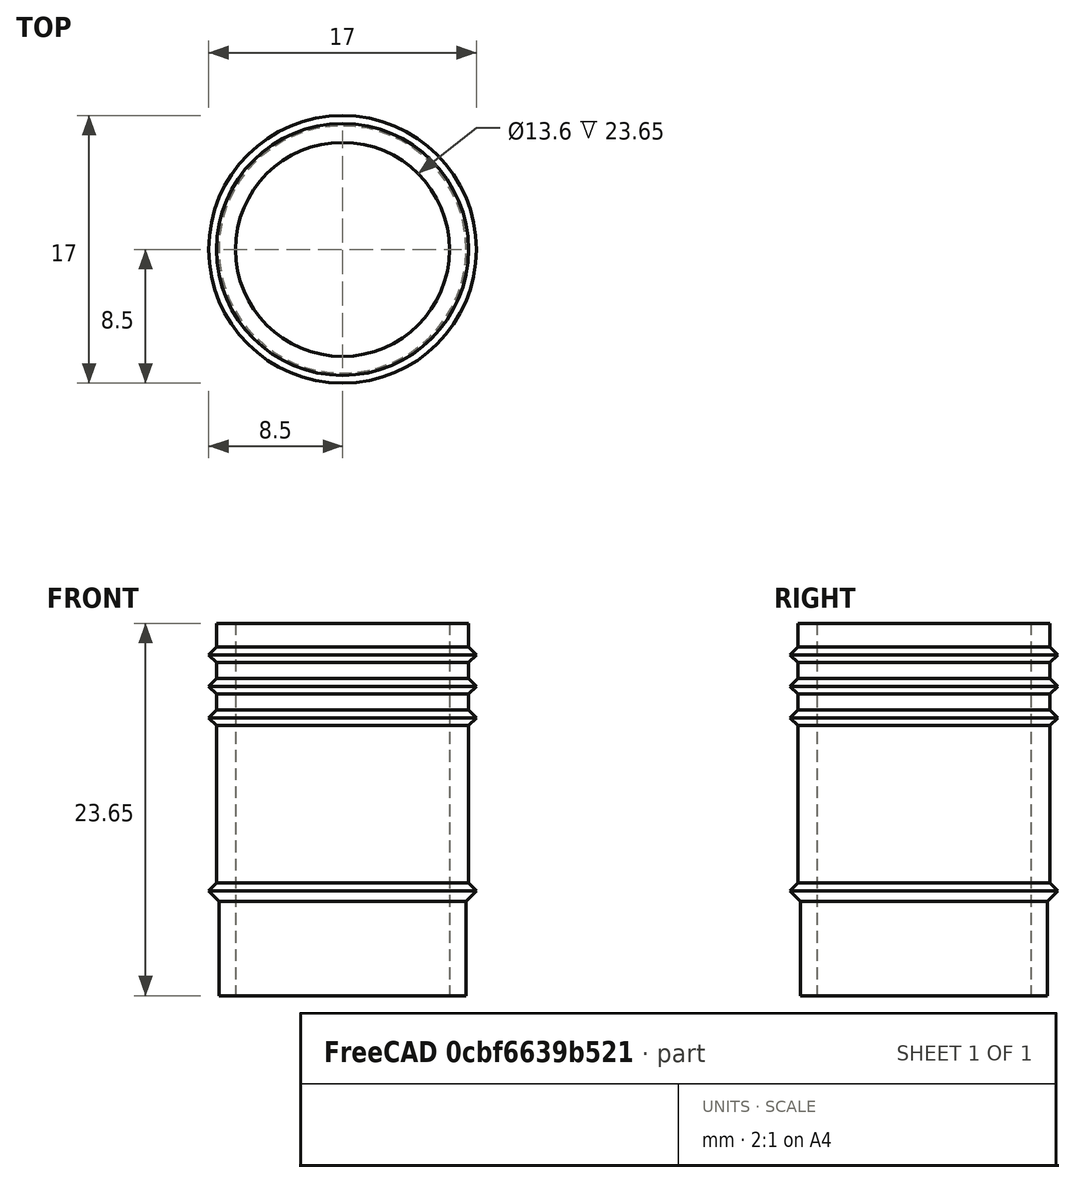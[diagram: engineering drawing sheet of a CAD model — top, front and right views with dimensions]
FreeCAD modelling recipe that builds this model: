
FCSTD DOCUMENT  (FreeCAD 0.18R4 (GitTag))
Label: hose_connector
License: All rights reserved
LicenseURL: http://en.wikipedia.org/wiki/All_rights_reserved
objects: Sketcher::SketchObject×1, Part::Revolution×1
note: 2 computed .brp shape members not serialized (recipe doc carries the construction recipe); baked Part::Feature solids carry a one-line shape summary decoded from their .brp

FEATURE [Sketcher::SketchObject] Sketch001
  MapMode = 5
  Placement = pos=(0,0,0) rot=(1,0,0;1.5708rad)
  sketch-geometry (16):
    g0: LineSegment StartX=8 StartY=17.15 StartZ=0 EndX=8.5 EndY=17.65 EndZ=0
    g1: LineSegment StartX=8.5 StartY=17.65 StartZ=0 EndX=8 EndY=18.15 EndZ=0
    g2: LineSegment StartX=8 StartY=18.15 StartZ=0 EndX=8 EndY=19.15 EndZ=0
    g3: LineSegment StartX=8 StartY=19.15 StartZ=0 EndX=8.5 EndY=19.65 EndZ=0
    g4: LineSegment StartX=8.5 StartY=19.65 StartZ=0 EndX=8 EndY=20.15 EndZ=0
    g5: LineSegment StartX=8 StartY=20.15 StartZ=0 EndX=8 EndY=21.15 EndZ=0
    g6: LineSegment StartX=8 StartY=21.15 StartZ=0 EndX=8.5 EndY=21.65 EndZ=0
    g7: LineSegment StartX=8.5 StartY=21.65 StartZ=0 EndX=8 EndY=22.15 EndZ=0
    g8: LineSegment StartX=8 StartY=22.15 StartZ=0 EndX=8 EndY=23.65 EndZ=0
    g9: LineSegment StartX=8 StartY=23.65 StartZ=0 EndX=6.8 EndY=23.65 EndZ=0
    g10: LineSegment StartX=6.8 StartY=23.65 StartZ=0 EndX=6.8 EndY=0 EndZ=0
    g11: LineSegment StartX=7.85 StartY=0 StartZ=0 EndX=6.8 EndY=0 EndZ=0
    g12: LineSegment StartX=8 StartY=17.15 StartZ=0 EndX=8 EndY=7.15 EndZ=0
    g13: LineSegment StartX=8 StartY=7.15 StartZ=0 EndX=8.5 EndY=6.65 EndZ=0
    g14: LineSegment StartX=8.5 StartY=6.65 StartZ=0 EndX=7.85 EndY=6 EndZ=0
    g15: LineSegment StartX=7.85 StartY=6 StartZ=0 EndX=7.85 EndY=0 EndZ=0
  constraints (48):
    c: Coincident(g0,g1)
    c: Coincident(g1,g2)
    c: Coincident(g2,g3)
    c: Coincident(g3,g4)
    c: Coincident(g4,g5)
    c: Vertical(g5)
    c: Coincident(g5,g6)
    c: Coincident(g6,g7)
    c: Coincident(g7,g8)
    c: Vertical(g8)
    c: Coincident(g8,g9)
    c: Coincident(g9,g10)
    c: Vertical(g10)
    c: Vertical(g2)
    c: Horizontal(g9)
    c: Vertical(g5,g7)
    c: Vertical(g4,g2)
    c: Vertical(g1,g0)
    c: Parallel(g0,g3)
    c: Parallel(g6,g3)
    c: Parallel(g4,g7)
    c: Parallel(g4,g1)
    c: Vertical(g3,g6)
    c: Vertical(g3,g0)
    c: DistanceX(g9,g9) = 1.2
    c: DistanceX(g1,g0) = 0.5
    c: DistanceX(g-1,g8) = 8
    c: DistanceY(g6,g8) = 2
    c: DistanceY(g3,g6) = 2
    c: Angle(g5,g6) = 2.35619
    c: Angle(g7,g6) = 1.5708
    c: DistanceY(g0,g3) = 2
    c: Horizontal(g11)
    c: Coincident(g10,g11)
    c: Coincident(g0,g12)
    c: Vertical(g12)
    c: Coincident(g12,g13)
    c: Coincident(g13,g14)
    c: Coincident(g14,g15)
    c: Coincident(g15,g11)
    c: Vertical(g15)
    c: Angle(g15,g14) = 2.35619
    c: Angle(g13,g12) = 2.35619
    c: DistanceY(g15,g15) = 6
    c: DistanceY(g-1,g10) = 0
    c: DistanceX(g12,g13) = 0.5
    c: DistanceY(g12,g12) = 10
    c: DistanceX(g-1,g11) = 7.85
FEATURE [Part::Revolution] Revolve
  Angle = 360
  Axis = (0,0,1)
  Base = (0,0,0)
  FaceMakerClass = Part::FaceMakerBullseye
  Solid = true
  Source = -> Sketch001
  Symmetric = false
